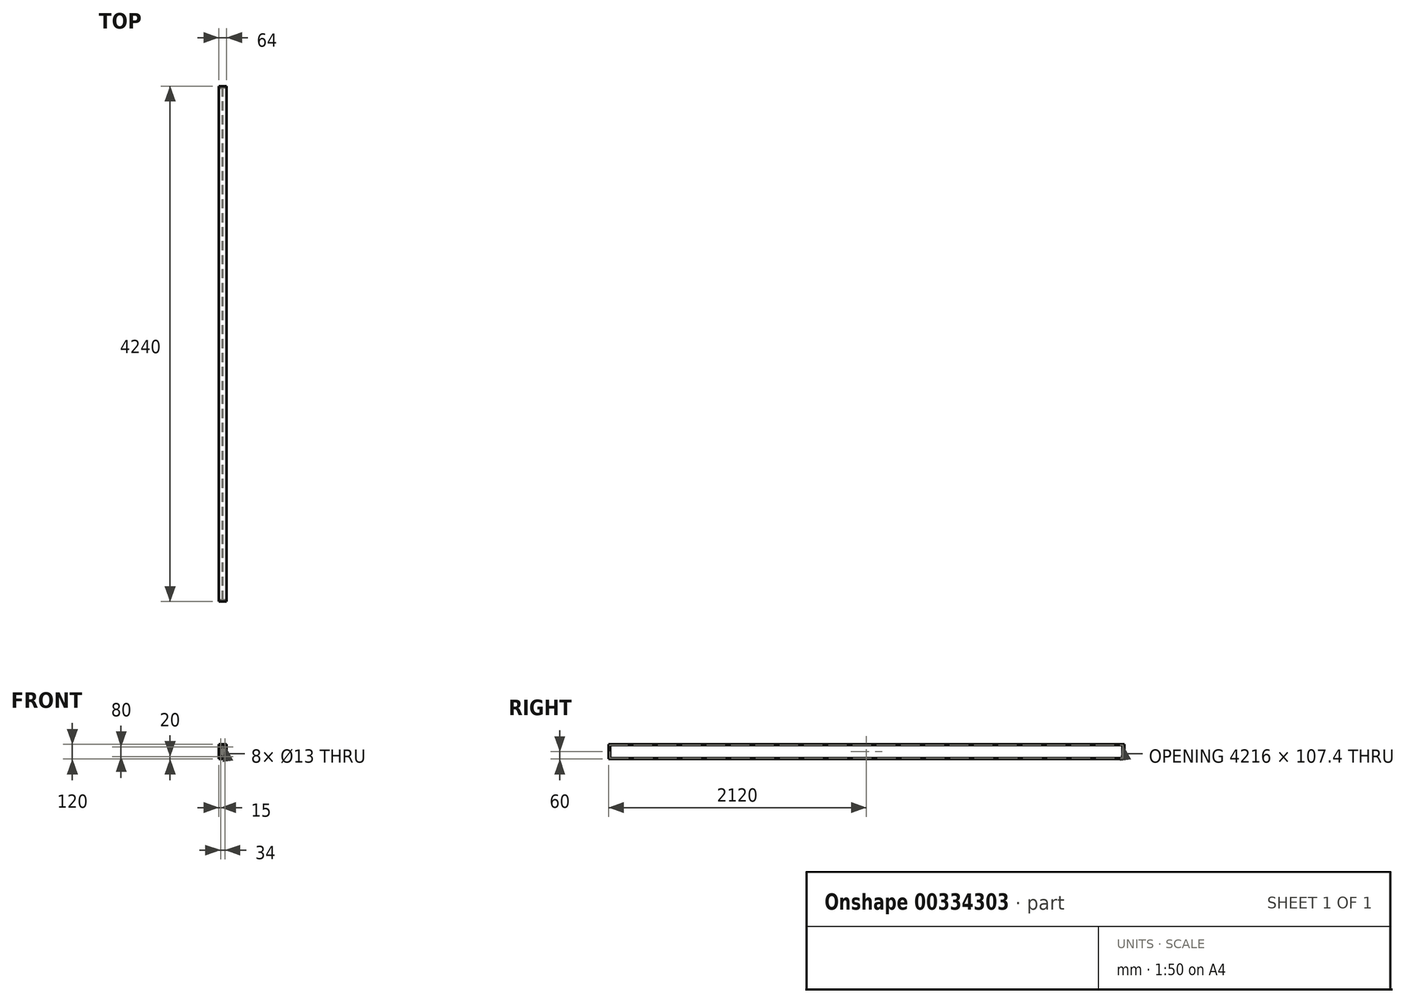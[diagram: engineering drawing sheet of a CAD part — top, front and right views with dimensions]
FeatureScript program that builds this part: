
annotation { "Feature Type Name" : "Feature", "Feature Type Description" : "" }
export const myFeature = defineFeature(function(context is Context, id is Id, definition is map)
    precondition{}
    {
        {
            var Q0;
            Q0=qCreatedBy(makeId("Front.planeOp"),FACE);
            var sketch = newSketch(context, id + "F0", { "sketchPlane" : qUnion([Q0])});
            skLineSegment(sketch, "E0", {"start": v(-32, 0) * mm, "end": v(32, 0) * mm});
            skLineSegment(sketch, "E1", {"start": v(32, 0) * mm, "end": v(32, 6.3) * mm});
            skLineSegment(sketch, "E2", {"start": v(32, 6.3) * mm, "end": v(9.2, 6.3) * mm});
            skLineSegment(sketch, "E3", {"start": v(2.2, 13.3) * mm, "end": v(2.2, 106.7) * mm});
            skLineSegment(sketch, "E4", {"start": v(9.2, 113.7) * mm, "end": v(32, 113.7) * mm});
            skLineSegment(sketch, "E5", {"start": v(32, 113.7) * mm, "end": v(32, 120) * mm});
            skLineSegment(sketch, "E6", {"start": v(32, 120) * mm, "end": v(-32, 120) * mm});
            skLineSegment(sketch, "E7", {"start": v(-32, 120) * mm, "end": v(-32, 113.7) * mm});
            skLineSegment(sketch, "E8", {"start": v(-32, 113.7) * mm, "end": v(-9.2, 113.7) * mm});
            skLineSegment(sketch, "E9", {"start": v(-2.2, 106.7) * mm, "end": v(-2.2, 13.3) * mm});
            skLineSegment(sketch, "E10", {"start": v(-9.2, 6.3) * mm, "end": v(-32, 6.3) * mm});
            skLineSegment(sketch, "E11", {"start": v(-32, 6.3) * mm, "end": v(-32, 0) * mm});
            skLineSegment(sketch, "E12", {"start": v(0, 0) * mm, "end": v(0, 0) * mm});
            skPoint(sketch, "E13.visualSharp", {"position": v(-2.2, 113.7) * mm});
            skArc(sketch, "E13.filletArc", {"start": v(-2.2, 106.7) * mm, "mid": v(-4.25, 111.65) * mm, "end": v(-9.2, 113.7) * mm});
            skPoint(sketch, "E14.visualSharp", {"position": v(-2.2, 6.3) * mm});
            skArc(sketch, "E14.filletArc", {"start": v(-9.2, 6.3) * mm, "mid": v(-4.25, 8.35) * mm, "end": v(-2.2, 13.3) * mm});
            skPoint(sketch, "E15.visualSharp", {"position": v(2.2, 6.3) * mm});
            skArc(sketch, "E15.filletArc", {"start": v(2.2, 13.3) * mm, "mid": v(4.25, 8.35) * mm, "end": v(9.2, 6.3) * mm});
            skPoint(sketch, "E16.visualSharp", {"position": v(2.2, 113.7) * mm});
            skArc(sketch, "E16.filletArc", {"start": v(9.2, 113.7) * mm, "mid": v(4.25, 111.65) * mm, "end": v(2.2, 106.7) * mm});
            skSolve(sketch);
        }
        {
            assignVariable(context, id + "F1", {"name" : "L_Pro", "anyValue" : 4240});
        }
        {
            var Q0;
            Q0=makeQuery(id+"F0.imprint","IMPRINT",FACE,{"disambiguationData":[TD([[makeQuery(id+"F0.imprint","IMPRINT",EDGE,{"derivedFrom":sQuery(id+"F0.wireOp",EDGE,"E0")}),1.0]])]});
            extrude(context, id + "F2", {"entities" : qUnion([Q0]), "depth" : (getVariable(context, 'L_Pro')) * mm});
        }
        {
            var Q0;
            Q0=makeQuery(id+"F2.opExtrude","CAP_FACE",FACE,{"disambiguationData":[OSD([sQuery(id+"F0.wireOp",EDGE,"E0"),sQuery(id+"F0.wireOp",EDGE,"E1"),sQuery(id+"F0.wireOp",EDGE,"E2"),sQuery(id+"F0.wireOp",EDGE,"E3"),sQuery(id+"F0.wireOp",EDGE,"E4"),sQuery(id+"F0.wireOp",EDGE,"E5"),sQuery(id+"F0.wireOp",EDGE,"E6"),sQuery(id+"F0.wireOp",EDGE,"E7"),sQuery(id+"F0.wireOp",EDGE,"E8"),sQuery(id+"F0.wireOp",EDGE,"E9"),sQuery(id+"F0.wireOp",EDGE,"E10"),sQuery(id+"F0.wireOp",EDGE,"E11"),sQuery(id+"F0.wireOp",EDGE,"E13.filletArc"),sQuery(id+"F0.wireOp",EDGE,"E14.filletArc"),sQuery(id+"F0.wireOp",EDGE,"E15.filletArc"),sQuery(id+"F0.wireOp",EDGE,"E16.filletArc")])],"isStart":true});
            var sketch = newSketch(context, id + "F3", { "sketchPlane" : qUnion([Q0])});
            skLineSegment(sketch, "E17.bottom", {"start": v(-32, 0) * mm, "end": v(32, 0) * mm});
            skLineSegment(sketch, "E17.top", {"start": v(-32, 120) * mm, "end": v(32, 120) * mm});
            skLineSegment(sketch, "E17.left", {"start": v(-32, 0) * mm, "end": v(-32, 120) * mm});
            skLineSegment(sketch, "E17.right", {"start": v(32, 0) * mm, "end": v(32, 120) * mm});
            skCircle(sketch, "E18", {"center": v(-17, 100) * mm, "radius": 6.5 * mm});
            skCircle(sketch, "E19", {"center": v(17, 100) * mm, "radius": 6.5 * mm});
            skCircle(sketch, "E20", {"center": v(17, 20) * mm, "radius": 6.5 * mm});
            skCircle(sketch, "E21", {"center": v(-17, 20) * mm, "radius": 6.5 * mm});
            skLineSegment(sketch, "E22", {"start": v(-17, 100) * mm, "end": v(17, 100) * mm, "construction": true});
            skLineSegment(sketch, "E23", {"start": v(-17, 20) * mm, "end": v(17, 20) * mm, "construction": true});
            skLineSegment(sketch, "E24", {"start": v(0, 120) * mm, "end": v(0, 0) * mm, "construction": true});
            skPoint(sketch, "E24.startSnap0", {"position": v(0, 120) * mm});
            skLineSegment(sketch, "E25", {"start": v(-32, 60) * mm, "end": v(32, 60) * mm, "construction": true});
            skSolve(sketch);
        }
        {
            var Q0;
            Q0=makeQuery(id+"F3.imprint","IMPRINT",FACE,{"disambiguationData":[TD([[makeQuery(id+"F3.imprint","IMPRINT",EDGE,{"derivedFrom":sQuery(id+"F3.wireOp",EDGE,"E19")}),-1.0]])]});
            var Q1;
            Q1=makeQuery(id+"F3.imprint","IMPRINT",FACE,{"disambiguationData":[TD([[makeQuery(id+"F3.imprint","IMPRINT",EDGE,{"derivedFrom":sQuery(id+"F3.wireOp",EDGE,"E18")}),-1.0]])]});
            var Q2;
            {var subQ3=sQuery(id+"F3.wireOp",EDGE,"E17.bottom");Q2=makeQuery(id+"F3.imprint","IMPRINT",FACE,{"disambiguationData":[TD([[makeQuery(id+"F3.imprint","IMPRINT",EDGE,{"derivedFrom":subQ3}),-1.0]])]});}
            extrude(context, id + "F4", {"entities" : qUnion([Q0, Q1, Q2]), "operationType" : NewBodyOperationType.ADD, "oppositeDirection" : true, "depth" : 12 * mm});
        }
        {
            var Q0;
            Q0=makeQuery(id+"F4.boolean.opBoolean","INTERSECT",EDGE,{"derivedFrom":[makeQuery(id+"F2.opExtrude","SWEPT_FACE",FACE,{"disambiguationData":[OSD([sQuery(id+"F0.wireOp",EDGE,"E4")])]}),makeQuery(id+"F4.opExtrude","CAP_FACE",FACE,{"disambiguationData":[OSD([sQuery(id+"F3.wireOp",EDGE,"E17.bottom"),sQuery(id+"F3.wireOp",EDGE,"E17.top"),sQuery(id+"F3.wireOp",EDGE,"E17.left"),sQuery(id+"F3.wireOp",EDGE,"E17.right"),sQuery(id+"F3.wireOp",EDGE,"E18"),sQuery(id+"F3.wireOp",EDGE,"E19"),sQuery(id+"F3.wireOp",EDGE,"E20"),sQuery(id+"F3.wireOp",EDGE,"E21")])],"isStart":false})]});
            var Q1;
            Q1=makeQuery(id+"F4.boolean.opBoolean","INTERSECT",EDGE,{"derivedFrom":[makeQuery(id+"F2.opExtrude","SWEPT_FACE",FACE,{"disambiguationData":[OSD([sQuery(id+"F0.wireOp",EDGE,"E16.filletArc")])]}),makeQuery(id+"F4.opExtrude","CAP_FACE",FACE,{"disambiguationData":[OSD([sQuery(id+"F3.wireOp",EDGE,"E17.bottom"),sQuery(id+"F3.wireOp",EDGE,"E17.top"),sQuery(id+"F3.wireOp",EDGE,"E17.left"),sQuery(id+"F3.wireOp",EDGE,"E17.right"),sQuery(id+"F3.wireOp",EDGE,"E18"),sQuery(id+"F3.wireOp",EDGE,"E19"),sQuery(id+"F3.wireOp",EDGE,"E20"),sQuery(id+"F3.wireOp",EDGE,"E21")])],"isStart":false})]});
            var Q2;
            Q2=makeQuery(id+"F4.boolean.opBoolean","INTERSECT",EDGE,{"derivedFrom":[makeQuery(id+"F2.opExtrude","SWEPT_FACE",FACE,{"disambiguationData":[OSD([sQuery(id+"F0.wireOp",EDGE,"E3")])]}),makeQuery(id+"F4.opExtrude","CAP_FACE",FACE,{"disambiguationData":[OSD([sQuery(id+"F3.wireOp",EDGE,"E17.bottom"),sQuery(id+"F3.wireOp",EDGE,"E17.top"),sQuery(id+"F3.wireOp",EDGE,"E17.left"),sQuery(id+"F3.wireOp",EDGE,"E17.right"),sQuery(id+"F3.wireOp",EDGE,"E18"),sQuery(id+"F3.wireOp",EDGE,"E19"),sQuery(id+"F3.wireOp",EDGE,"E20"),sQuery(id+"F3.wireOp",EDGE,"E21")])],"isStart":false})]});
            var Q3;
            Q3=makeQuery(id+"F4.boolean.opBoolean","INTERSECT",EDGE,{"derivedFrom":[makeQuery(id+"F2.opExtrude","SWEPT_FACE",FACE,{"disambiguationData":[OSD([sQuery(id+"F0.wireOp",EDGE,"E15.filletArc")])]}),makeQuery(id+"F4.opExtrude","CAP_FACE",FACE,{"disambiguationData":[OSD([sQuery(id+"F3.wireOp",EDGE,"E17.bottom"),sQuery(id+"F3.wireOp",EDGE,"E17.top"),sQuery(id+"F3.wireOp",EDGE,"E17.left"),sQuery(id+"F3.wireOp",EDGE,"E17.right"),sQuery(id+"F3.wireOp",EDGE,"E18"),sQuery(id+"F3.wireOp",EDGE,"E19"),sQuery(id+"F3.wireOp",EDGE,"E20"),sQuery(id+"F3.wireOp",EDGE,"E21")])],"isStart":false})]});
            var Q4;
            Q4=makeQuery(id+"F4.boolean.opBoolean","INTERSECT",EDGE,{"derivedFrom":[makeQuery(id+"F2.opExtrude","SWEPT_FACE",FACE,{"disambiguationData":[OSD([sQuery(id+"F0.wireOp",EDGE,"E2")])]}),makeQuery(id+"F4.opExtrude","CAP_FACE",FACE,{"disambiguationData":[OSD([sQuery(id+"F3.wireOp",EDGE,"E17.bottom"),sQuery(id+"F3.wireOp",EDGE,"E17.top"),sQuery(id+"F3.wireOp",EDGE,"E17.left"),sQuery(id+"F3.wireOp",EDGE,"E17.right"),sQuery(id+"F3.wireOp",EDGE,"E18"),sQuery(id+"F3.wireOp",EDGE,"E19"),sQuery(id+"F3.wireOp",EDGE,"E20"),sQuery(id+"F3.wireOp",EDGE,"E21")])],"isStart":false})]});
            chamfer(context, id + "F5", {"entities" : qUnion([Q0, Q1, Q2, Q3, Q4]), "width" : 3 * mm, "tangentPropagation" : true});
        }
        {
            var Q0;
            Q0=makeQuery(id+"F4.boolean.opBoolean","INTERSECT",EDGE,{"derivedFrom":[makeQuery(id+"F2.opExtrude","SWEPT_FACE",FACE,{"disambiguationData":[OSD([sQuery(id+"F0.wireOp",EDGE,"E10")])]}),makeQuery(id+"F4.opExtrude","CAP_FACE",FACE,{"disambiguationData":[OSD([sQuery(id+"F3.wireOp",EDGE,"E17.bottom"),sQuery(id+"F3.wireOp",EDGE,"E17.top"),sQuery(id+"F3.wireOp",EDGE,"E17.left"),sQuery(id+"F3.wireOp",EDGE,"E17.right"),sQuery(id+"F3.wireOp",EDGE,"E18"),sQuery(id+"F3.wireOp",EDGE,"E19"),sQuery(id+"F3.wireOp",EDGE,"E20"),sQuery(id+"F3.wireOp",EDGE,"E21")])],"isStart":false})]});
            var Q1;
            Q1=makeQuery(id+"F4.boolean.opBoolean","INTERSECT",EDGE,{"derivedFrom":[makeQuery(id+"F2.opExtrude","SWEPT_FACE",FACE,{"disambiguationData":[OSD([sQuery(id+"F0.wireOp",EDGE,"E14.filletArc")])]}),makeQuery(id+"F4.opExtrude","CAP_FACE",FACE,{"disambiguationData":[OSD([sQuery(id+"F3.wireOp",EDGE,"E17.bottom"),sQuery(id+"F3.wireOp",EDGE,"E17.top"),sQuery(id+"F3.wireOp",EDGE,"E17.left"),sQuery(id+"F3.wireOp",EDGE,"E17.right"),sQuery(id+"F3.wireOp",EDGE,"E18"),sQuery(id+"F3.wireOp",EDGE,"E19"),sQuery(id+"F3.wireOp",EDGE,"E20"),sQuery(id+"F3.wireOp",EDGE,"E21")])],"isStart":false})]});
            var Q2;
            Q2=makeQuery(id+"F4.boolean.opBoolean","INTERSECT",EDGE,{"derivedFrom":[makeQuery(id+"F2.opExtrude","SWEPT_FACE",FACE,{"disambiguationData":[OSD([sQuery(id+"F0.wireOp",EDGE,"E9")])]}),makeQuery(id+"F4.opExtrude","CAP_FACE",FACE,{"disambiguationData":[OSD([sQuery(id+"F3.wireOp",EDGE,"E17.bottom"),sQuery(id+"F3.wireOp",EDGE,"E17.top"),sQuery(id+"F3.wireOp",EDGE,"E17.left"),sQuery(id+"F3.wireOp",EDGE,"E17.right"),sQuery(id+"F3.wireOp",EDGE,"E18"),sQuery(id+"F3.wireOp",EDGE,"E19"),sQuery(id+"F3.wireOp",EDGE,"E20"),sQuery(id+"F3.wireOp",EDGE,"E21")])],"isStart":false})]});
            var Q3;
            Q3=makeQuery(id+"F4.boolean.opBoolean","INTERSECT",EDGE,{"derivedFrom":[makeQuery(id+"F2.opExtrude","SWEPT_FACE",FACE,{"disambiguationData":[OSD([sQuery(id+"F0.wireOp",EDGE,"E13.filletArc")])]}),makeQuery(id+"F4.opExtrude","CAP_FACE",FACE,{"disambiguationData":[OSD([sQuery(id+"F3.wireOp",EDGE,"E17.bottom"),sQuery(id+"F3.wireOp",EDGE,"E17.top"),sQuery(id+"F3.wireOp",EDGE,"E17.left"),sQuery(id+"F3.wireOp",EDGE,"E17.right"),sQuery(id+"F3.wireOp",EDGE,"E18"),sQuery(id+"F3.wireOp",EDGE,"E19"),sQuery(id+"F3.wireOp",EDGE,"E20"),sQuery(id+"F3.wireOp",EDGE,"E21")])],"isStart":false})]});
            var Q4;
            Q4=makeQuery(id+"F4.boolean.opBoolean","INTERSECT",EDGE,{"derivedFrom":[makeQuery(id+"F2.opExtrude","SWEPT_FACE",FACE,{"disambiguationData":[OSD([sQuery(id+"F0.wireOp",EDGE,"E8")])]}),makeQuery(id+"F4.opExtrude","CAP_FACE",FACE,{"disambiguationData":[OSD([sQuery(id+"F3.wireOp",EDGE,"E17.bottom"),sQuery(id+"F3.wireOp",EDGE,"E17.top"),sQuery(id+"F3.wireOp",EDGE,"E17.left"),sQuery(id+"F3.wireOp",EDGE,"E17.right"),sQuery(id+"F3.wireOp",EDGE,"E18"),sQuery(id+"F3.wireOp",EDGE,"E19"),sQuery(id+"F3.wireOp",EDGE,"E20"),sQuery(id+"F3.wireOp",EDGE,"E21")])],"isStart":false})]});
            chamfer(context, id + "F6", {"entities" : qUnion([Q0, Q1, Q2, Q3, Q4]), "width" : 3 * mm, "tangentPropagation" : true});
        }
        {
            var Q0;
            Q0=qSketchRegion(id+"F3",true);
            extrude(context, id + "F7", {"entities" : qUnion([Q0]), "operationType" : NewBodyOperationType.ADD, "oppositeDirection" : true, "depth" : (getVariable(context, 'L_Pro')) * mm, "hasSecondDirection" : true, "secondDirectionOppositeDirection" : true, "secondDirectionDepth" : (getVariable(context, 'L_Pro') - 12) * mm});
        }
        {
            var Q0;
            Q0=makeQuery(id+"F7.boolean.opBoolean","INTERSECT",EDGE,{"derivedFrom":[makeQuery(id+"F2.opExtrude","SWEPT_FACE",FACE,{"disambiguationData":[OSD([sQuery(id+"F0.wireOp",EDGE,"E4")])]}),makeQuery(id+"F7.opExtrude","CAP_FACE",FACE,{"disambiguationData":[OSD([sQuery(id+"F3.wireOp",EDGE,"E17.bottom"),sQuery(id+"F3.wireOp",EDGE,"E17.top"),sQuery(id+"F3.wireOp",EDGE,"E17.left"),sQuery(id+"F3.wireOp",EDGE,"E17.right"),sQuery(id+"F3.wireOp",EDGE,"E18"),sQuery(id+"F3.wireOp",EDGE,"E19"),sQuery(id+"F3.wireOp",EDGE,"E20"),sQuery(id+"F3.wireOp",EDGE,"E21")])],"isStart":true})]});
            var Q1;
            Q1=makeQuery(id+"F7.boolean.opBoolean","INTERSECT",EDGE,{"derivedFrom":[makeQuery(id+"F2.opExtrude","SWEPT_FACE",FACE,{"disambiguationData":[OSD([sQuery(id+"F0.wireOp",EDGE,"E16.filletArc")])]}),makeQuery(id+"F7.opExtrude","CAP_FACE",FACE,{"disambiguationData":[OSD([sQuery(id+"F3.wireOp",EDGE,"E17.bottom"),sQuery(id+"F3.wireOp",EDGE,"E17.top"),sQuery(id+"F3.wireOp",EDGE,"E17.left"),sQuery(id+"F3.wireOp",EDGE,"E17.right"),sQuery(id+"F3.wireOp",EDGE,"E18"),sQuery(id+"F3.wireOp",EDGE,"E19"),sQuery(id+"F3.wireOp",EDGE,"E20"),sQuery(id+"F3.wireOp",EDGE,"E21")])],"isStart":true})]});
            var Q2;
            Q2=makeQuery(id+"F7.boolean.opBoolean","INTERSECT",EDGE,{"derivedFrom":[makeQuery(id+"F2.opExtrude","SWEPT_FACE",FACE,{"disambiguationData":[OSD([sQuery(id+"F0.wireOp",EDGE,"E3")])]}),makeQuery(id+"F7.opExtrude","CAP_FACE",FACE,{"disambiguationData":[OSD([sQuery(id+"F3.wireOp",EDGE,"E17.bottom"),sQuery(id+"F3.wireOp",EDGE,"E17.top"),sQuery(id+"F3.wireOp",EDGE,"E17.left"),sQuery(id+"F3.wireOp",EDGE,"E17.right"),sQuery(id+"F3.wireOp",EDGE,"E18"),sQuery(id+"F3.wireOp",EDGE,"E19"),sQuery(id+"F3.wireOp",EDGE,"E20"),sQuery(id+"F3.wireOp",EDGE,"E21")])],"isStart":true})]});
            var Q3;
            Q3=makeQuery(id+"F7.boolean.opBoolean","INTERSECT",EDGE,{"derivedFrom":[makeQuery(id+"F2.opExtrude","SWEPT_FACE",FACE,{"disambiguationData":[OSD([sQuery(id+"F0.wireOp",EDGE,"E15.filletArc")])]}),makeQuery(id+"F7.opExtrude","CAP_FACE",FACE,{"disambiguationData":[OSD([sQuery(id+"F3.wireOp",EDGE,"E17.bottom"),sQuery(id+"F3.wireOp",EDGE,"E17.top"),sQuery(id+"F3.wireOp",EDGE,"E17.left"),sQuery(id+"F3.wireOp",EDGE,"E17.right"),sQuery(id+"F3.wireOp",EDGE,"E18"),sQuery(id+"F3.wireOp",EDGE,"E19"),sQuery(id+"F3.wireOp",EDGE,"E20"),sQuery(id+"F3.wireOp",EDGE,"E21")])],"isStart":true})]});
            var Q4;
            Q4=makeQuery(id+"F7.boolean.opBoolean","INTERSECT",EDGE,{"derivedFrom":[makeQuery(id+"F2.opExtrude","SWEPT_FACE",FACE,{"disambiguationData":[OSD([sQuery(id+"F0.wireOp",EDGE,"E2")])]}),makeQuery(id+"F7.opExtrude","CAP_FACE",FACE,{"disambiguationData":[OSD([sQuery(id+"F3.wireOp",EDGE,"E17.bottom"),sQuery(id+"F3.wireOp",EDGE,"E17.top"),sQuery(id+"F3.wireOp",EDGE,"E17.left"),sQuery(id+"F3.wireOp",EDGE,"E17.right"),sQuery(id+"F3.wireOp",EDGE,"E18"),sQuery(id+"F3.wireOp",EDGE,"E19"),sQuery(id+"F3.wireOp",EDGE,"E20"),sQuery(id+"F3.wireOp",EDGE,"E21")])],"isStart":true})]});
            chamfer(context, id + "F8", {"entities" : qUnion([Q0, Q1, Q2, Q3, Q4]), "width" : 3 * mm, "tangentPropagation" : true});
        }
        {
            var Q0;
            Q0=makeQuery(id+"F7.boolean.opBoolean","INTERSECT",EDGE,{"derivedFrom":[makeQuery(id+"F2.opExtrude","SWEPT_FACE",FACE,{"disambiguationData":[OSD([sQuery(id+"F0.wireOp",EDGE,"E8")])]}),makeQuery(id+"F7.opExtrude","CAP_FACE",FACE,{"disambiguationData":[OSD([sQuery(id+"F3.wireOp",EDGE,"E17.bottom"),sQuery(id+"F3.wireOp",EDGE,"E17.top"),sQuery(id+"F3.wireOp",EDGE,"E17.left"),sQuery(id+"F3.wireOp",EDGE,"E17.right"),sQuery(id+"F3.wireOp",EDGE,"E18"),sQuery(id+"F3.wireOp",EDGE,"E19"),sQuery(id+"F3.wireOp",EDGE,"E20"),sQuery(id+"F3.wireOp",EDGE,"E21")])],"isStart":true})]});
            var Q1;
            Q1=makeQuery(id+"F7.boolean.opBoolean","INTERSECT",EDGE,{"derivedFrom":[makeQuery(id+"F2.opExtrude","SWEPT_FACE",FACE,{"disambiguationData":[OSD([sQuery(id+"F0.wireOp",EDGE,"E13.filletArc")])]}),makeQuery(id+"F7.opExtrude","CAP_FACE",FACE,{"disambiguationData":[OSD([sQuery(id+"F3.wireOp",EDGE,"E17.bottom"),sQuery(id+"F3.wireOp",EDGE,"E17.top"),sQuery(id+"F3.wireOp",EDGE,"E17.left"),sQuery(id+"F3.wireOp",EDGE,"E17.right"),sQuery(id+"F3.wireOp",EDGE,"E18"),sQuery(id+"F3.wireOp",EDGE,"E19"),sQuery(id+"F3.wireOp",EDGE,"E20"),sQuery(id+"F3.wireOp",EDGE,"E21")])],"isStart":true})]});
            var Q2;
            Q2=makeQuery(id+"F7.boolean.opBoolean","INTERSECT",EDGE,{"derivedFrom":[makeQuery(id+"F2.opExtrude","SWEPT_FACE",FACE,{"disambiguationData":[OSD([sQuery(id+"F0.wireOp",EDGE,"E9")])]}),makeQuery(id+"F7.opExtrude","CAP_FACE",FACE,{"disambiguationData":[OSD([sQuery(id+"F3.wireOp",EDGE,"E17.bottom"),sQuery(id+"F3.wireOp",EDGE,"E17.top"),sQuery(id+"F3.wireOp",EDGE,"E17.left"),sQuery(id+"F3.wireOp",EDGE,"E17.right"),sQuery(id+"F3.wireOp",EDGE,"E18"),sQuery(id+"F3.wireOp",EDGE,"E19"),sQuery(id+"F3.wireOp",EDGE,"E20"),sQuery(id+"F3.wireOp",EDGE,"E21")])],"isStart":true})]});
            var Q3;
            Q3=makeQuery(id+"F7.boolean.opBoolean","INTERSECT",EDGE,{"derivedFrom":[makeQuery(id+"F2.opExtrude","SWEPT_FACE",FACE,{"disambiguationData":[OSD([sQuery(id+"F0.wireOp",EDGE,"E14.filletArc")])]}),makeQuery(id+"F7.opExtrude","CAP_FACE",FACE,{"disambiguationData":[OSD([sQuery(id+"F3.wireOp",EDGE,"E17.bottom"),sQuery(id+"F3.wireOp",EDGE,"E17.top"),sQuery(id+"F3.wireOp",EDGE,"E17.left"),sQuery(id+"F3.wireOp",EDGE,"E17.right"),sQuery(id+"F3.wireOp",EDGE,"E18"),sQuery(id+"F3.wireOp",EDGE,"E19"),sQuery(id+"F3.wireOp",EDGE,"E20"),sQuery(id+"F3.wireOp",EDGE,"E21")])],"isStart":true})]});
            var Q4;
            Q4=makeQuery(id+"F7.boolean.opBoolean","INTERSECT",EDGE,{"derivedFrom":[makeQuery(id+"F2.opExtrude","SWEPT_FACE",FACE,{"disambiguationData":[OSD([sQuery(id+"F0.wireOp",EDGE,"E10")])]}),makeQuery(id+"F7.opExtrude","CAP_FACE",FACE,{"disambiguationData":[OSD([sQuery(id+"F3.wireOp",EDGE,"E17.bottom"),sQuery(id+"F3.wireOp",EDGE,"E17.top"),sQuery(id+"F3.wireOp",EDGE,"E17.left"),sQuery(id+"F3.wireOp",EDGE,"E17.right"),sQuery(id+"F3.wireOp",EDGE,"E18"),sQuery(id+"F3.wireOp",EDGE,"E19"),sQuery(id+"F3.wireOp",EDGE,"E20"),sQuery(id+"F3.wireOp",EDGE,"E21")])],"isStart":true})]});
            chamfer(context, id + "F9", {"entities" : qUnion([Q0, Q1, Q2, Q3, Q4]), "width" : 3 * mm, "tangentPropagation" : true});
        }
    });
